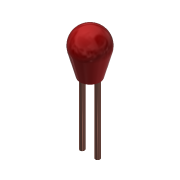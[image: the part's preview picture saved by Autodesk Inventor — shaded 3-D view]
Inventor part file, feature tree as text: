
AUTODESK INVENTOR PART (.ipt)
format: ipt  version: 2017 (Build 210142000, 142)  size: 126,976 bytes
history: native  units: in
note: dims shown in document units (in); Inventor stores cm internally (conversion verified against a paired STEP export)
features: sketch x2, revolve x1, extrude x1
ambient origin geometry x8: Origin, YZ Plane, XZ Plane, XY Plane, X Axis, Y Axis, Z Axis, Center Point
bodies: Solid1 (feature_tree)
feature tree (4):
  revolve  "Revolution1"  [1 undecoded]
  extrude  "Extrusion1"  TaperAngle=90.0deg  [1 undecoded]
  sketch  "Sketch1"  dims[d0=0.015in d1=0.065in]
  sketch  "Sketch2"  dims[d2=0.025in d3=90.0deg d4=0.007in d5=0.03in d6=0.1in d7=0.0in]
note: 2 required parameter values undecoded (feature->parameter linkage not recoverable at this tier; creation-order binding heuristic only, values carry confidence <= 0.55)